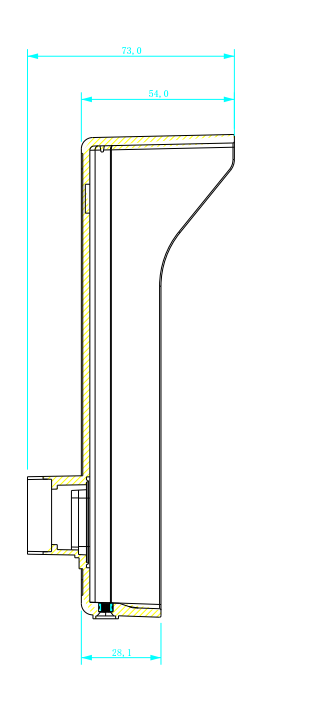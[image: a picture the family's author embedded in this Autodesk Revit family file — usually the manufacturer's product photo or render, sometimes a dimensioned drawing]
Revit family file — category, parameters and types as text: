
# Revit family: AU-04LAF
name_source: partatom
category: Устройства связи
units: mm (PartAtom-declared; Revit-internal decimal feet)

## family parameters
Всегда вертикально = Нет
На основе рабочей плоскости = Да
Общий = Да
При загрузке вырезать с полостями = Нет
Размер круглого соединителя = Использовать диаметр
Сохранять ориентацию аннотаций = Нет
Тип детали = Нормальный
Точка расчета площади = Нет

## types (1)
- AU-04LAF
    ADSK_URL документации изделия = https://cdn.bas-ip.com
    ADSK_URL страницы изделия = https://bas-ip.com
    ADSK_Версия Revit = Revit 2020
    ADSK_Единица измерения = шт
    ADSK_Завод-изготовитель = BAS-IP
    ADSK_Классификация нагрузок = Внутренний монитор индивидуальный
    ADSK_Количество фаз = 1
    ADSK_Коэффициент мощности = 0.9
    ADSK_Марка = AU-04LAF
    ADSK_Наименование = Внутренний монитор индивидуальный AU-04LAF
    ADSK_Наименование краткое = AU-04LAF
    ADSK_Напряжение = 12 В
    ADSK_Номинальная мощность = 3 Вт
    ADSK_Полная мощность = 3 В·А
    ADSK_Размер_Длина = 185 мм
    ADSK_Размер_Толщина = 30 мм
    ADSK_Размер_Ширина = 135 мм
    BIM library = https://bimlib.ru
    URL = https://www.bas-ip.ru
    Встроенная камера = Нет
    Габаритные размеры (без SP-AU) = 135×185×30 мм
    Голосовая почта = Нет
    Группа модели = Внутренний монитор индивидуальный
    Дисплей = 4,3-дюймовый TFT LCD, сенсорный, емкостный
    Дополнительно = Подключение кнопки звонка; SIP P2P; Управляемый выход при поступлении входящего звонка
    Изготовитель = BAS-IP
    Изображение типоразмера = <Нет>
    Интерфейс = Мультиязычный, графический
    Количество IP-камер = до 8 камер
    Количество индивидуальных вызывных панелей = до 9 панелей
    Количество многоквартирных вызывных панелей = до 9 панелей
    Корпус = пластик
    Модуль Wi-Fi = Да
    Мощность = 6 Вт, в режиме ожидания — 2,5 Вт
    Обновление программного обеспечения = через Ethernet
    Общий вес = 0,61 кг
    Описание = Самый бюджетный IP видеодомофон в линейке BAS-IP. Одной из особенностей AU-04LAF является возможность подключения дополнительной трубки SP-AU. Это решение идеально подходит для тех, кто желает конфиденциальности в разговорах. Управление домофоном возможно с помощью механических клавиш и сенсорного экрана. Классический черный и белый цвет корпуса подойдут для любого стиля интерьера. Мониторы AU-04LAF не поддерживают работу с вызывными панелями второй версии (v2).
    Отметка по умолчанию = 0 мм
    Память = Запись фото во внутреннюю память
    Поддержка получения сообщений = Да
    Подключение дополнительных мониторов = До 5 мониторов
    Просмотр IP-камер в режиме ожидания = Да
    Рабочая влажность = 20–80 %
    Рабочая температура = -10 – +55 °С
    Размеры коробки = 233×168,5×65 мм
    Разрешение экрана = 480×272
    Режим фоторамки = Нет
    Сигнализация = 4 входа для датчиков
    Сценарии = Нет
    Тип домофона = Видеодомофон
    Тип установки = Настенный монтаж
    Управление домашней автоматикой = свет, шторы, лифт
    Цветовое решение = белый, черный
    Электропитание = PoE, +12 В постоянного тока (+11%-6%)
